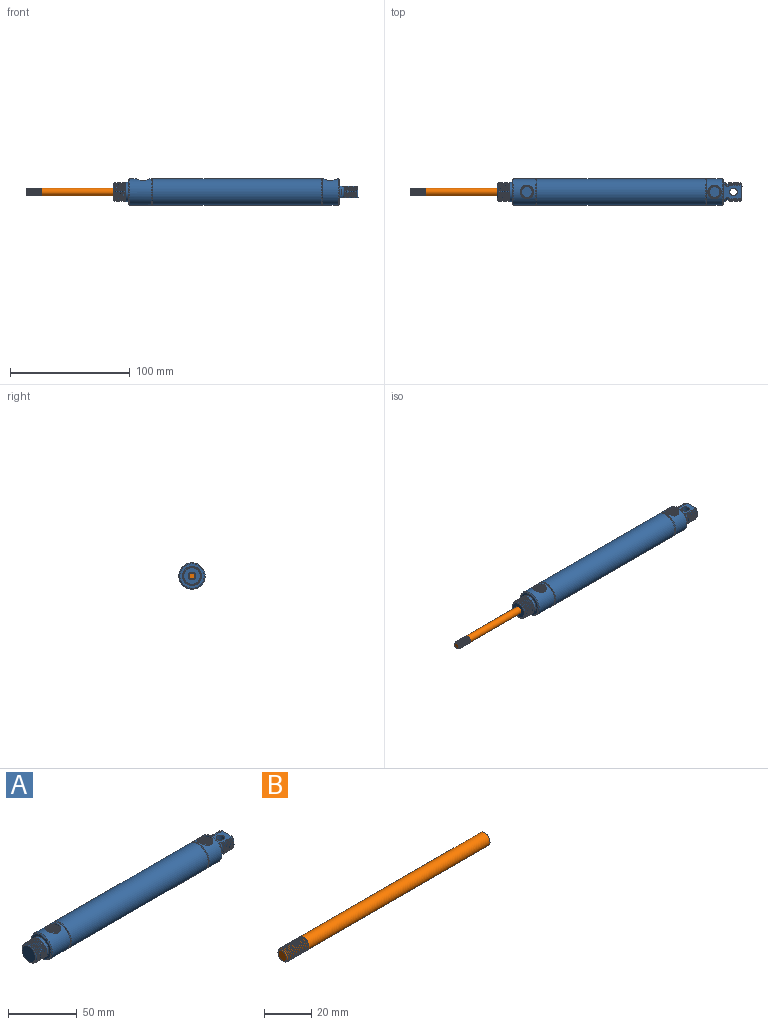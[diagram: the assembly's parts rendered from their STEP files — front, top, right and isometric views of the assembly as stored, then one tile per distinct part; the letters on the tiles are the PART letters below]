
ASSEMBLY  parts=2 mates=1
PART A: 127 faces, bbox 205.6x22.4x22.4 mm
  f0: cone r=5.14mm half-angle=45deg, axis (0,0,1), area 13.3mm2, adj f116,f122,f123,f124
  f1: cone r=5.14mm half-angle=45deg, axis (0,0,1), area 13.3mm2, adj f113,f117,f118,f119
  f2: cylinder r=10.92mm len=21.84mm, axis (-1,0,0), area 782mm2, adj f13,f14,f114,f115
  f3: cylinder r=10.92mm len=21.84mm, axis (-1,0,0), area 1155.5mm2, adj f8,f10,f111,f112
  f4: plane 20.32x20.32mm, normal (1,0,0), area 181.1mm2, adj f14,f32,f94,f95,f96
  f5: cylinder r=10.92mm len=140.53mm, axis (-1,0,0), area 9644mm2, adj f6,f11
  f6: cone r=10.65mm half-angle=26.6deg, axis (1,0,0), area 41.4mm2, adj f5,f7
  f7: plane 21.3x21.3mm, normal (-1,0,0), area 18mm2, adj f6,f8
  f8: cone r=10.92mm half-angle=45deg, axis (-1,0,0), area 51.7mm2, adj f3,f7
  f9: plane 20.32x20.32mm, normal (-1,0,0), area 126.4mm2, adj f10,f104
  f10: cone r=10.16mm half-angle=45deg, axis (1,0,0), area 71.4mm2, adj f3,f9
  f11: cone r=10.92mm half-angle=26.6deg, axis (-1,0,0), area 41.4mm2, adj f5,f12
  f12: plane 21.3x21.3mm, normal (1,0,0), area 18mm2, adj f11,f13
  f13: cone r=10.38mm half-angle=45deg, axis (1,0,0), area 51.7mm2, adj f2,f12
  f14: cone r=10.92mm half-angle=45deg, axis (-1,0,0), area 71.4mm2, adj f2,f4
  f15: bspline ~5.61x2.97mm, area 0mm2, adj f16,f31,f96
  f16: bspline ~9.93x2.06mm, area 0.6mm2, adj f15,f27,f31,f96
  f17: cylinder r=7.94mm len=9.65mm, axis (1,0,0), area 1.8mm2, adj f23,f25,f95,f96
  f18: bspline ~9.93x2.06mm, area 1.9mm2, adj f21,f24,f95,f96
  f19: bspline ~9.93x2.06mm, area 1.9mm2, adj f22,f25,f95,f96
  f20: bspline ~9.93x2.06mm, area 1.9mm2, adj f23,f67,f95,f96
  f21: bspline ~11.23x2.97mm, area 9.8mm2, adj f18,f62,f95,f96
  f22: bspline ~11.23x2.97mm, area 11.2mm2, adj f19,f28,f95,f96
  f23: bspline ~11.23x2.97mm, area 11.2mm2, adj f17,f20,f95,f96
  f24: bspline ~11.23x2.97mm, area 11.2mm2, adj f18,f28,f95,f96
  f25: bspline ~11.23x2.97mm, area 11.2mm2, adj f17,f19,f95,f96
  f26: cylinder r=7.94mm len=9.65mm, axis (1,0,0), area 1.8mm2, adj f27,f51,f95,f96
  f27: bspline ~11.23x2.97mm, area 9.9mm2, adj f16,f26,f31,f95,f96
  f28: cylinder r=7.94mm len=9.65mm, axis (1,0,0), area 1.8mm2, adj f22,f24,f95,f96
  f29: cone r=6.88mm half-angle=45deg, axis (-1,0,0), area 7.5mm2, adj f41,f64,f95,f96
  f30: plane 9.72x2.78mm, normal (1,0,0), area 9.2mm2, adj f47,f48,f49,f94,f95,f96
  f31: torus R=7.56mm, axis (-1,0,0), area 33.8mm2, adj f15,f16,f27,f91,f95,f96
  f32: cylinder r=7.94mm len=9.65mm, axis (1,0,0), area 23.7mm2, adj f4,f91,f95,f96
  f33: cylinder r=7.94mm len=1.02mm, axis (1,0,0), area 0mm2, adj f34,f93,f95
  f34: bspline ~11.23x2.97mm, area 8.7mm2, adj f33,f35,f92,f93,f95,f96
  f35: bspline ~9.93x2.06mm, area 1.9mm2, adj f34,f52,f95,f96
  f36: cylinder r=7.94mm len=9.65mm, axis (1,0,0), area 1.8mm2, adj f46,f70,f95,f96
  f37: cylinder r=7.94mm len=9.65mm, axis (1,0,0), area 1.8mm2, adj f43,f45,f95,f96
  f38: bspline ~9.93x2.06mm, area 1.9mm2, adj f41,f44,f95,f96
  f39: bspline ~9.93x2.06mm, area 1.9mm2, adj f42,f45,f95,f96
  f40: bspline ~9.93x2.06mm, area 1.9mm2, adj f43,f46,f95,f96
  f41: bspline ~11.23x2.97mm, area 4.4mm2, adj f29,f38,f95,f96
  f42: bspline ~11.23x2.97mm, area 11.2mm2, adj f39,f61,f95,f96
  f43: bspline ~11.23x2.97mm, area 11.2mm2, adj f37,f40,f95,f96
  f44: bspline ~11.23x2.97mm, area 11.2mm2, adj f38,f61,f95,f96
  f45: bspline ~11.23x2.97mm, area 11.2mm2, adj f37,f39,f95,f96
  f46: bspline ~11.23x2.97mm, area 11.2mm2, adj f36,f40,f95,f96
  f47: bspline ~9.93x2.06mm, area 0.6mm2, adj f30,f48,f49,f92,f95
  f48: bspline ~11.23x2.97mm, area 0.7mm2, adj f30,f47,f92,f96
  f49: bspline ~5.61x2.97mm, area 0.1mm2, adj f30,f47,f95
  f50: cylinder r=7.94mm len=9.65mm, axis (1,0,0), area 1.8mm2, adj f52,f89,f95,f96
  f51: bspline ~11.23x2.97mm, area 11.2mm2, adj f26,f53,f95,f96
  f52: bspline ~11.23x2.97mm, area 11.2mm2, adj f35,f50,f95,f96
  f53: bspline ~9.93x2.06mm, area 1.9mm2, adj f51,f90,f95,f96
  f54: cylinder r=7.94mm len=9.65mm, axis (1,0,0), area 1.8mm2, adj f67,f73,f95,f96
  f55: cylinder r=7.94mm len=9.65mm, axis (1,0,0), area 1.8mm2, adj f71,f76,f95,f96
  f56: cylinder r=7.94mm len=9.65mm, axis (1,0,0), area 1.8mm2, adj f74,f79,f95,f96
  f57: cylinder r=7.94mm len=9.65mm, axis (1,0,0), area 1.8mm2, adj f77,f82,f95,f96
  f58: cylinder r=7.94mm len=9.65mm, axis (1,0,0), area 1.8mm2, adj f80,f85,f95,f96
  f59: cylinder r=7.94mm len=9.65mm, axis (1,0,0), area 1.8mm2, adj f83,f88,f95,f96
  f60: cylinder r=7.94mm len=9.65mm, axis (1,0,0), area 1.8mm2, adj f86,f90,f95,f96
  f61: cylinder r=7.94mm len=9.65mm, axis (1,0,0), area 1.8mm2, adj f42,f44,f95,f96
  f62: cone r=6.88mm half-angle=45deg, axis (-1,0,0), area 12mm2, adj f21,f64,f65,f66,f68,f95,f96
  f63: cylinder r=3.17mm len=9.65mm, axis (0,0,1), area 192.5mm2, adj f95,f96
  f64: plane 13.76x9.65mm, normal (1,0,0), area 120.9mm2, adj f29,f62,f95,f96
  f65: bspline ~9.93x2.06mm, area 0.7mm2, adj f62,f66,f68,f95
  f66: bspline ~5.61x2.97mm, area 0mm2, adj f62,f65,f95
  f67: bspline ~11.23x2.97mm, area 11.2mm2, adj f20,f54,f95,f96
  f68: bspline ~11.23x2.97mm, area 1.7mm2, adj f62,f65,f95
  f69: bspline ~9.93x2.06mm, area 1.9mm2, adj f70,f71,f95,f96
  f70: bspline ~11.23x2.97mm, area 11.2mm2, adj f36,f69,f95,f96
  f71: bspline ~11.23x2.97mm, area 11.2mm2, adj f55,f69,f95,f96
  f72: bspline ~9.93x2.06mm, area 1.9mm2, adj f73,f74,f95,f96
  f73: bspline ~11.23x2.97mm, area 11.2mm2, adj f54,f72,f95,f96
  f74: bspline ~11.23x2.97mm, area 11.2mm2, adj f56,f72,f95,f96
  f75: bspline ~9.93x2.06mm, area 1.9mm2, adj f76,f77,f95,f96
  f76: bspline ~11.23x2.97mm, area 11.2mm2, adj f55,f75,f95,f96
  f77: bspline ~11.23x2.97mm, area 11.2mm2, adj f57,f75,f95,f96
  f78: bspline ~9.93x2.06mm, area 1.9mm2, adj f79,f80,f95,f96
  f79: bspline ~11.23x2.97mm, area 11.2mm2, adj f56,f78,f95,f96
  f80: bspline ~11.23x2.97mm, area 11.2mm2, adj f58,f78,f95,f96
  f81: bspline ~9.93x2.06mm, area 1.9mm2, adj f82,f83,f95,f96
  f82: bspline ~11.23x2.97mm, area 11.2mm2, adj f57,f81,f95,f96
  f83: bspline ~11.23x2.97mm, area 11.2mm2, adj f59,f81,f95,f96
  f84: bspline ~9.93x2.06mm, area 1.9mm2, adj f85,f86,f95,f96
  f85: bspline ~11.23x2.97mm, area 11.2mm2, adj f58,f84,f95,f96
  f86: bspline ~11.23x2.97mm, area 11.2mm2, adj f60,f84,f95,f96
  f87: bspline ~9.93x2.06mm, area 1.9mm2, adj f88,f89,f95,f96
  f88: bspline ~11.23x2.97mm, area 11.2mm2, adj f59,f87,f95,f96
  f89: bspline ~11.23x2.97mm, area 11.2mm2, adj f50,f87,f95,f96
  f90: bspline ~11.23x2.97mm, area 11.2mm2, adj f53,f60,f95,f96
  f91: plane 9.65x2.12mm, normal (1,0,0), area 4mm2, adj f31,f32,f95,f96
  f92: torus R=7.56mm, axis (-1,0,0), area 33.6mm2, adj f34,f47,f48,f93,f95,f96
  f93: plane 8.4x2.06mm, normal (-1,0,0), area 1.9mm2, adj f33,f34,f92,f95
  f94: cylinder r=7.94mm len=9.65mm, axis (1,0,0), area 23.7mm2, adj f4,f30,f95,f96
  f95: plane 15.81x12.66mm, normal (0,0,1), area 145.2mm2, adj f4,f17,f18,f19,f20,f21,f22,f23
  f96: plane 15.81x12.66mm, normal (0,0,-1), area 144.8mm2, adj f4,f15,f16,f17,f18,f19,f20,f21
  f97: plane 16.45x16.45mm, normal (-1,0,0), area 21.9mm2, adj f104,f106,f107,f108
  f98: cylinder r=7.94mm len=15.88mm, axis (1,0,0), area 8.8mm2, adj f99,f105,f106,f108
  f99: cylinder r=7.94mm len=15.88mm, axis (1,0,0), area 8.8mm2, adj f98,f100,f106,f108
  f100: cylinder r=7.94mm len=15.88mm, axis (1,0,0), area 8.8mm2, adj f99,f101,f106,f108
  f101: cylinder r=7.94mm len=15.88mm, axis (1,0,0), area 8.8mm2, adj f100,f102,f106,f108
  f102: cylinder r=7.94mm len=15.88mm, axis (1,0,0), area 8.8mm2, adj f101,f103,f106,f108
  f103: cylinder r=7.94mm len=15.88mm, axis (1,0,0), area 8.8mm2, adj f102,f104,f106,f108
  f104: cylinder r=7.94mm len=15.88mm, axis (1,0,0), area 119mm2, adj f9,f97,f103,f106,f108
  f105: cylinder r=7.94mm len=5.61mm, axis (1,0,0), area 0.6mm2, adj f98,f108,f110
  f106: bspline ~15.88x15.88mm, area 345.7mm2, adj f97,f98,f99,f100,f101,f102,f103,f104
  f107: bspline ~14.04x14.04mm, area 56.6mm2, adj f97,f106,f108,f110
  f108: bspline ~15.88x15.88mm, area 317mm2, adj f97,f98,f99,f100,f101,f102,f103,f104
  f109: plane 13.76x13.76mm, normal (-1,0,0), area 148.7mm2, adj f110
  f110: cone r=7.94mm half-angle=45deg, axis (1,0,0), area 38.7mm2, adj f105,f106,f107,f108,f109
  f111: cylinder r=5.66mm len=11.32mm, axis (0,0,-1), area 14mm2, adj f3,f113
  f112: cylinder r=5.66mm len=11.32mm, axis (0,0,-1), area 14mm2, adj f3,f113
  f113: plane 11.32x11.32mm, normal (0,0,1), area 17.5mm2, adj f1,f111,f112,f120
  f114: cylinder r=5.66mm len=11.32mm, axis (0,0,-1), area 0mm2, adj f2,f116
  f115: cylinder r=5.66mm len=11.32mm, axis (0,0,-1), area 0mm2, adj f2,f116
  f116: plane 11.32x11.32mm, normal (0,0,1), area 17.5mm2, adj f0,f114,f115,f125
  f117: bspline ~10.29x10.29mm, area 126.3mm2, adj f1,f118,f120,f121
  f118: bspline ~9.07x9.07mm, area 18.6mm2, adj f1,f117,f119,f121
  f119: bspline ~10.29x10.29mm, area 126.4mm2, adj f1,f118,f120,f121
  f120: cylinder r=5.14mm len=10.29mm, axis (0,0,1), area 23.6mm2, adj f113,f117,f119,f121
  f121: plane 10.09x10.09mm, normal (0,0,1), area 73.7mm2, adj f117,f118,f119,f120
  f122: bspline ~10.29x10.29mm, area 126.3mm2, adj f0,f123,f125,f126
  f123: bspline ~9.07x9.07mm, area 18.6mm2, adj f0,f122,f124,f126
  f124: bspline ~10.29x10.29mm, area 126.4mm2, adj f0,f123,f125,f126
  f125: cylinder r=5.14mm len=10.29mm, axis (0,0,1), area 23.6mm2, adj f116,f122,f124,f126
  f126: plane 10.09x10.09mm, normal (0,0,1), area 73.7mm2, adj f122,f123,f124,f125
PART B: 21 faces, bbox 121.3x6.7x6.7 mm
  f0: cylinder r=3.17mm len=6.35mm, axis (-1,0,0), area 1.3mm2, adj f1,f15,f16,f18
  f1: cylinder r=3.17mm len=6.35mm, axis (-1,0,0), area 2.3mm2, adj f0,f2,f16,f18
  f2: cylinder r=3.17mm len=6.35mm, axis (-1,0,0), area 2.3mm2, adj f1,f3,f16,f18
  f3: cylinder r=3.17mm len=6.35mm, axis (-1,0,0), area 2.3mm2, adj f2,f4,f16,f18
  f4: cylinder r=3.17mm len=6.35mm, axis (-1,0,0), area 2.3mm2, adj f3,f5,f16,f18
  f5: cylinder r=3.17mm len=6.35mm, axis (-1,0,0), area 2.3mm2, adj f4,f6,f16,f18
  f6: cylinder r=3.17mm len=6.35mm, axis (-1,0,0), area 2.3mm2, adj f5,f7,f16,f18
  f7: cylinder r=3.17mm len=6.35mm, axis (-1,0,0), area 2.3mm2, adj f6,f8,f16,f18
  f8: cylinder r=3.17mm len=6.35mm, axis (-1,0,0), area 2.3mm2, adj f7,f9,f16,f18
  f9: cylinder r=3.17mm len=6.35mm, axis (-1,0,0), area 2.3mm2, adj f8,f10,f16,f18
  f10: cylinder r=3.17mm len=6.35mm, axis (-1,0,0), area 2.3mm2, adj f9,f11,f16,f18
  f11: cylinder r=3.17mm len=6.35mm, axis (-1,0,0), area 2.3mm2, adj f10,f12,f16,f18
  f12: cylinder r=3.17mm len=6.35mm, axis (-1,0,0), area 2.3mm2, adj f11,f13,f16,f18
  f13: cylinder r=3.17mm len=108.63mm, axis (-1,0,0), area 2155.1mm2, adj f12,f16,f18,f19,f20
  f14: plane 4.99x4.99mm, normal (-1,0,0), area 19.6mm2, adj f15
  f15: cone r=2.49mm half-angle=45deg, axis (1,0,0), area 9.4mm2, adj f0,f14,f16,f17,f18
  f16: bspline ~13.04x6.35mm, area 167.1mm2, adj f0,f1,f2,f3,f4,f5,f6,f7
  f17: bspline ~12.93x5.17mm, area 25.6mm2, adj f15,f16,f18,f19
  f18: bspline ~13.49x6.35mm, area 166.4mm2, adj f0,f1,f2,f3,f4,f5,f6,f7
  f19: plane 6.71x6.71mm, normal (-1,0,0), area 5.5mm2, adj f13,f16,f17,f18
  f20: plane 6.35x6.35mm, normal (1,0,0), area 31.7mm2, adj f13
PLACE A t=(-48.76,18.52,-28.3)mm fixed
PLACE B t=(-7.29,18.52,-28.3)mm
MATE slider B.f0 <-> A.f6  axis (1,0,0) through (-96.57,18.52,-28.3)mm
